# Revit family: CM-XBOX-INLINE2
name_source: partatom
category: Mechanical Equipment
revit_build: Autodesk Revit 2015 (Build: 20140606_1530(x64)
units: mm (PartAtom-declared; Revit-internal decimal feet)

## types (1)
- CM-XBOX-INLINE2
    Apparent Load = 644 VA
    Catalogue Pages = http://www.nuaire.info
    Classification.Uniclass.Pr.Description = Air cooled condensing units
    Classification.Uniclass.Pr.Number = Pr_70_65_03_02
    Description = Inline Cooling Module
    Duct Connection Height = 90 mm  [stored 0.295276 ft]
    Duct Connection Width = 220 mm  [stored 0.721785 ft]
    Electrical Phase = 1
    Fan Unit = No
    Fax Number = +44(0)2920-858-222
    Full Load Current = 3 A
    Height = 365 mm
    I&M Manual = http://nuaire.info
    IFCExportAs = IfcCondenserType
    Length = 610 mm
    Manufacturer = Nuaire
    Manufacturer Name = Nuaire
    Maximum Ambient Temperature = 40 °C
    Model = CM-XBOX-INLINE
    Nuaire Model Code = CM-XBOX-INLINE
    Nuaire Model No = CM-XBOX-INLINE
    Number of Connection Poles = 2
    OmniClass Number = 23-33 37 00
    OmniClass Title = Refrigerant Condensing Units
    Postcode = CF83 1NA
    Revit Family Last Revised = 10/01/2020
    Starting Current = 3 A
    Supplier Part No = CM-XBOX-INLINE
    Telephone Number = +44(0)2920-858-200
    Type Comments = Inline Cooling Module
    URL = http://www.nuaire.co.uk
    Unit Description = Inline Cooling Module
    VAT Registration Number = 877308
    Voltage = 230 V
    Warranty Period = 1 Years
    Weatherproof or Internal Only = Internal
    Weight = 47.00 kg
    Width = 923 mm

note: [stored X ft] marks values corroborated as IEEE doubles in the binary element streams (Revit-internal decimal feet)

## geometry (parser evidence)
native form markers: Blend x13, Sweep x7
no freeform markers — native parametric forms only
